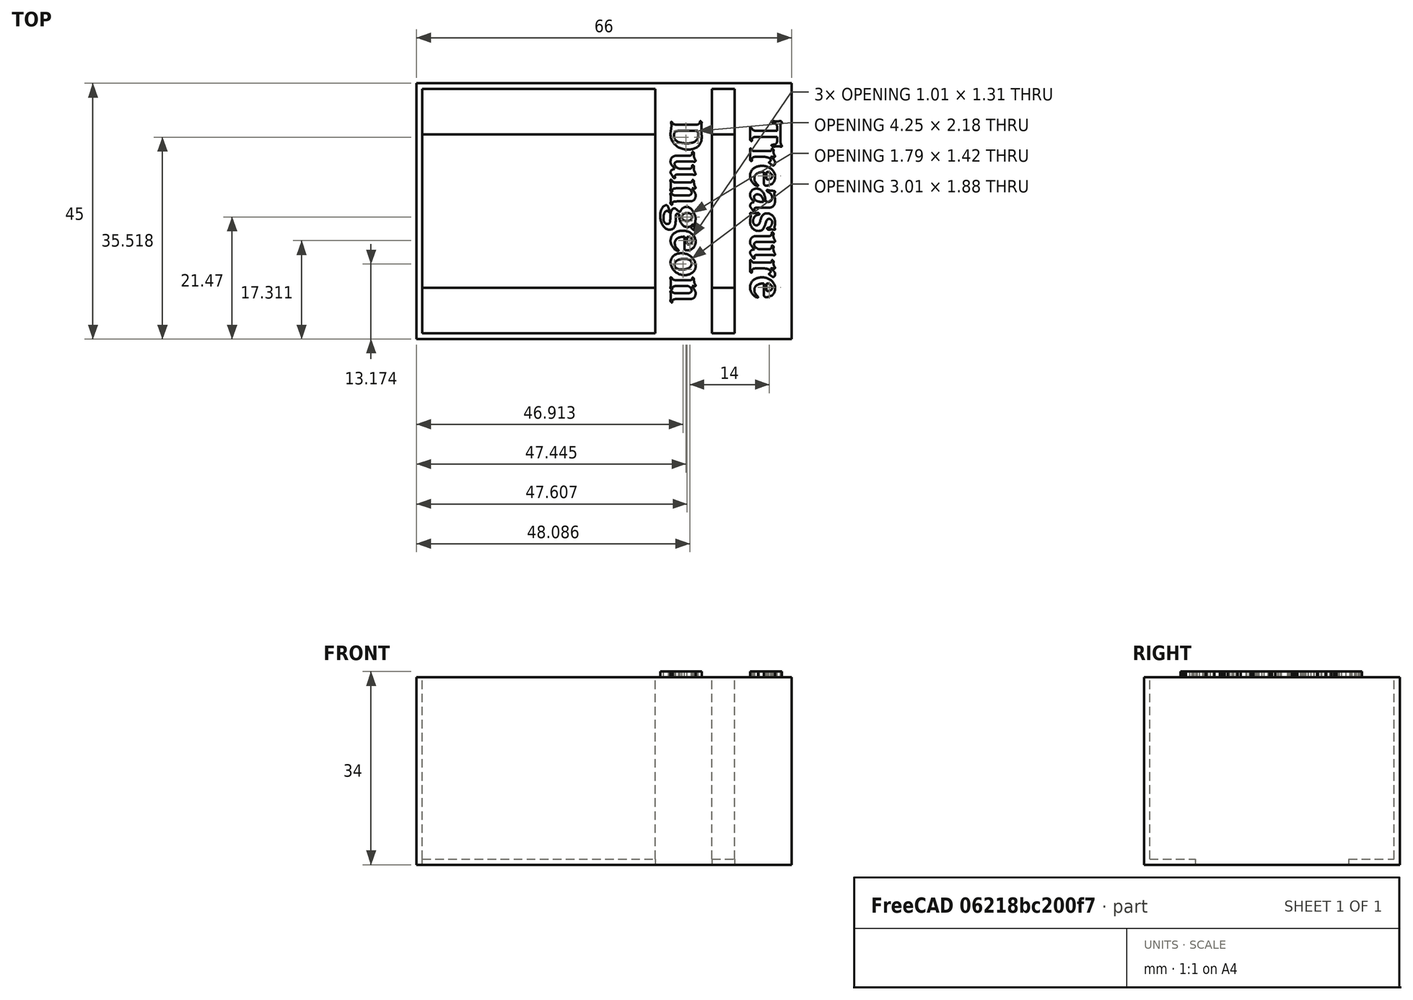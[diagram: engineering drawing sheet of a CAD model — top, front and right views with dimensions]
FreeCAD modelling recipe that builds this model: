
FCSTD DOCUMENT  (FreeCAD 0.18R4 (GitTag))
Label: dungeon
License: All rights reserved
LicenseURL: http://en.wikipedia.org/wiki/All_rights_reserved
objects: Part::Box×8, Part::MultiFuse×4, Part::Cut×2, Part::Part2DObjectPython×2, Part::Extrusion×2
note: 18 computed .brp shape members not serialized (recipe doc carries the construction recipe); baked Part::Feature solids carry a one-line shape summary decoded from their .brp

FEATURE [Part::Box] Box  label="Cube"
  AttacherType = Attacher::AttachEngine3D
  Height = 33
  Length = 202
  Placement = pos=(0,-1,0) rot=(0,0,1;0rad)
  Width = 45
FEATURE [Part::Box] Box001  label="Cube001"
  AttacherType = Attacher::AttachEngine3D
  Height = 33
  Length = 200
  Placement = pos=(1,0,0) rot=(0,0,1;0rad)
  Width = 43
FEATURE [Part::Cut] Cut
  Base = -> Box
  Tool = -> Box001
FEATURE [Part::Box] Box002  label="Cube002"
  AttacherType = Attacher::AttachEngine3D
  Height = 1
  Length = 202
  Width = 8
FEATURE [Part::Box] Box003  label="Cube003"
  AttacherType = Attacher::AttachEngine3D
  Height = 1
  Length = 202
  Placement = pos=(0,35,0) rot=(0,0,1;0rad)
  Width = 8
FEATURE [Part::MultiFuse] Fusion
  Shapes = -> [Cut,Box002,Box003]
FEATURE [Part::Box] Box004  label="Cube004"
  AttacherType = Attacher::AttachEngine3D
  Height = 33
  Length = 10
  Placement = pos=(42,0,0) rot=(0,0,1;0rad)
  Width = 43
FEATURE [Part::Box] Box005  label="Cube005"
  AttacherType = Attacher::AttachEngine3D
  Height = 33
  Length = 10
  Placement = pos=(58,0,0) rot=(0,0,1;0rad)
  Width = 43
FEATURE [Part::Box] Box006  label="Cube006"
  AttacherType = Attacher::AttachEngine3D
  Height = 33
  Length = 143
  Placement = pos=(66,-1,0) rot=(0,0,1;0rad)
  Width = 45
FEATURE [Part::MultiFuse] Fusion001
  Shapes = -> [Fusion,Box004,Box005]
FEATURE [Part::Cut] Cut001
  Base = -> Fusion001
  Tool = -> Box006
FEATURE [Part::Part2DObjectPython] ShapeString  # Draft 2D object (typed FeaturePython)
  FontFile = <userpath>/Downloads/talisman/Caxton Bold.otf
  Placement = pos=(45.54,20.86,33) rot=(0,0,1;0rad)
  Size = 3
  String = Treasure
  Tracking = 0
FEATURE [Part::Part2DObjectPython] ShapeString001  # Draft 2D object (typed FeaturePython)
  FontFile = <userpath>/Downloads/talisman/Caxton Bold.otf
  Placement = pos=(45.54,20.86,33) rot=(0,0,1;0rad)
  Size = 3
  String = Dungeon
  Tracking = 0
FEATURE [Part::Box] Box007  label="Cube007"
  AttacherType = Attacher::AttachEngine3D
  Height = 33
  Length = 10
  Placement = pos=(56,0,0) rot=(0,0,1;0rad)
  Width = 43
FEATURE [Part::MultiFuse] Fusion002
  Shapes = -> [Cut001,Box007]
FEATURE [Part::Extrusion] Extrude
  Base = -> ShapeString
  Dir = (0,0,1)
  DirMode = 2
  FaceMakerClass = Part::FaceMakerBullseye
  LengthFwd = 1
  LengthRev = 0
  Placement = pos=(38,83,0) rot=(0,0,-1;1.5708rad)
  Solid = false
  Symmetric = false
FEATURE [Part::Extrusion] Extrude001
  Base = -> ShapeString001
  Dir = (0,0,1)
  DirMode = 2
  FaceMakerClass = Part::FaceMakerBullseye
  LengthFwd = 1
  LengthRev = 0
  Placement = pos=(24,83,0) rot=(0,0,-1;1.5708rad)
  Solid = false
  Symmetric = false
FEATURE [Part::MultiFuse] Fusion003
  Shapes = -> [Extrude,Extrude001]
